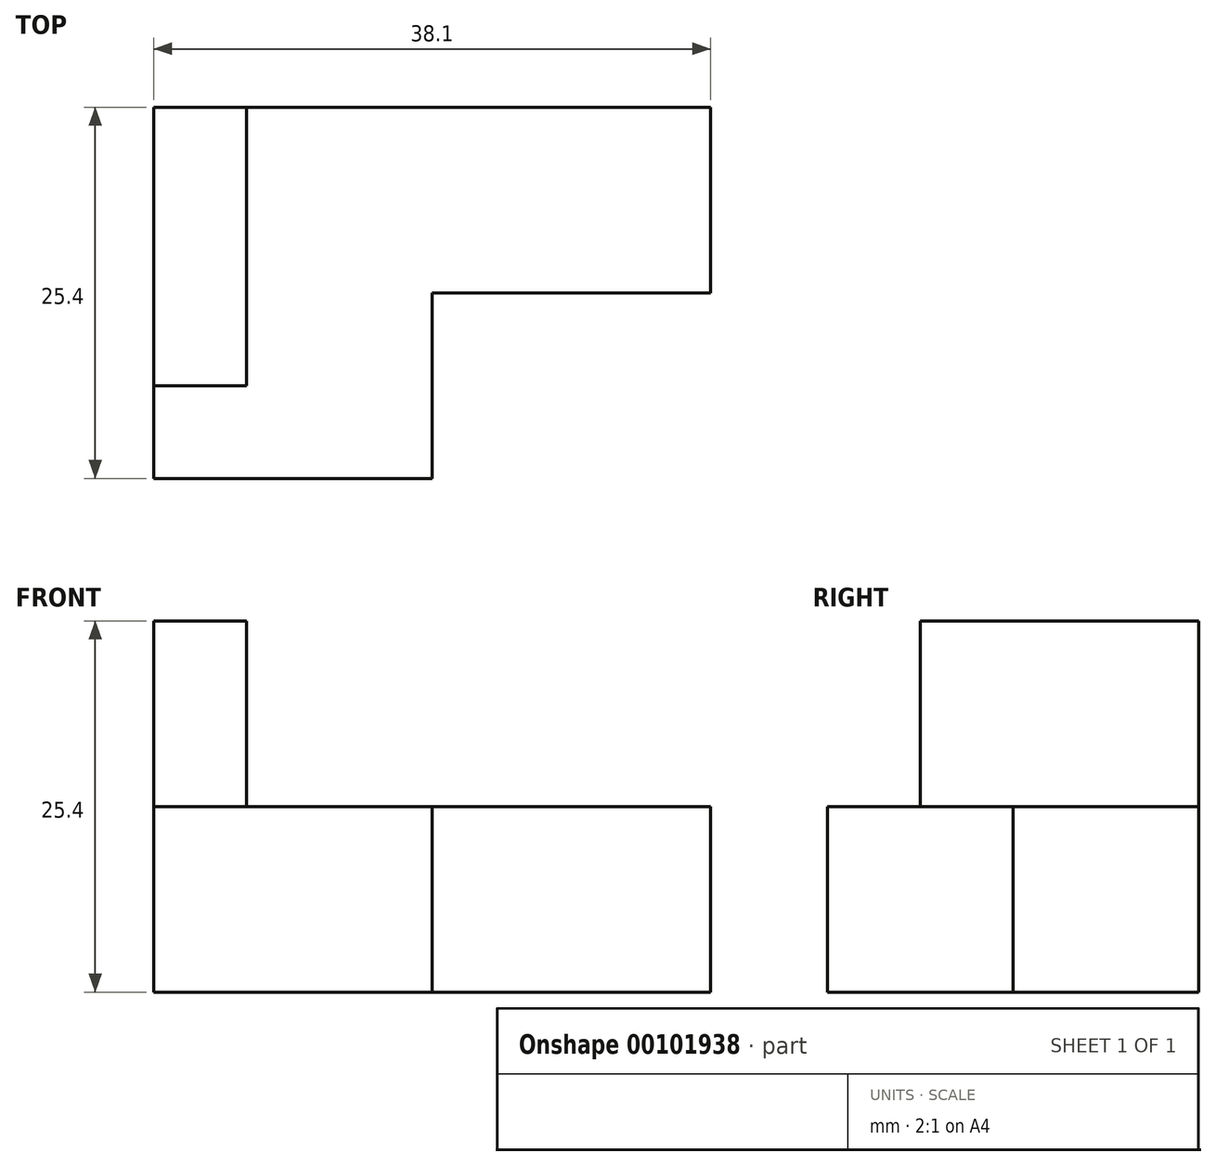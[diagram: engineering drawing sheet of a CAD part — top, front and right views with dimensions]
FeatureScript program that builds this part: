
annotation { "Feature Type Name" : "Feature", "Feature Type Description" : "" }
export const myFeature = defineFeature(function(context is Context, id is Id, definition is map)
    precondition{}
    {
        {
            var Q0;
            Q0=qCreatedBy(makeId("Front.planeOp"),FACE);
            var sketch = newSketch(context, id + "F0", { "sketchPlane" : qUnion([Q0])});
            skLineSegment(sketch, "E0", {"start": v(0, 0) * mm, "end": v(38.1, 0) * mm});
            skLineSegment(sketch, "E1", {"start": v(38.1, 0) * mm, "end": v(38.1, 12.7) * mm});
            skLineSegment(sketch, "E2", {"start": v(38.1, 12.7) * mm, "end": v(6.35, 12.7) * mm});
            skLineSegment(sketch, "E3", {"start": v(6.35, 12.7) * mm, "end": v(6.35, 25.4) * mm});
            skLineSegment(sketch, "E4", {"start": v(6.35, 25.4) * mm, "end": v(0, 25.4) * mm});
            skLineSegment(sketch, "E5", {"start": v(0, 25.4) * mm, "end": v(0, 0) * mm});
            skSolve(sketch);
        }
        {
            var Q0;
            Q0 = qSketchRegion(id + "F0", true);
            extrude(context, id + "F1", {"entities" : qUnion([Q0]), "endBound" : BoundingType.SYMMETRIC, "depth" : 25.4 * mm});
        }
        {
            var Q0;
            Q0=makeQuery(id+"F1.opExtrude","SWEPT_FACE",FACE,{"disambiguationData":[OSD([sQuery(id+"F0.wireOp",EDGE,"E2")])]});
            var sketch = newSketch(context, id + "F2", { "sketchPlane" : qUnion([Q0])});
            skLineSegment(sketch, "E6.bottom", {"start": v(38.1, -12.7) * mm, "end": v(19.05, -12.7) * mm});
            skLineSegment(sketch, "E6.top", {"start": v(38.1, 0) * mm, "end": v(19.05, 0) * mm});
            skLineSegment(sketch, "E6.left", {"start": v(38.1, -12.7) * mm, "end": v(38.1, 0) * mm});
            skLineSegment(sketch, "E6.right", {"start": v(19.05, -12.7) * mm, "end": v(19.05, 0) * mm});
            skSolve(sketch);
        }
        {
            var Q0;
            Q0=makeQuery(id+"F2.imprint","IMPRINT",FACE,{"disambiguationData":[TD([[makeQuery(id+"F2.imprint","IMPRINT",EDGE,{"derivedFrom":sQuery(id+"F2.wireOp",EDGE,"E6.bottom")}),-1.0]])]});
            extrude(context, id + "F3", {"entities" : qUnion([Q0]), "operationType" : NewBodyOperationType.REMOVE, "endBound" : BoundingType.THROUGH_ALL, "oppositeDirection" : true, "depth" : 25.4 * mm});
        }
        {
            var Q0;
            Q0=makeQuery(id+"F1.opExtrude","SWEPT_FACE",FACE,{"disambiguationData":[OSD([sQuery(id+"F0.wireOp",EDGE,"E3")])]});
            var sketch = newSketch(context, id + "F4", { "sketchPlane" : qUnion([Q0])});
            skLineSegment(sketch, "E7.bottom", {"start": v(-12.7, 25.4) * mm, "end": v(-6.35, 25.4) * mm});
            skLineSegment(sketch, "E7.top", {"start": v(-12.7, 12.7) * mm, "end": v(-6.35, 12.7) * mm});
            skLineSegment(sketch, "E7.left", {"start": v(-12.7, 25.4) * mm, "end": v(-12.7, 12.7) * mm});
            skLineSegment(sketch, "E7.right", {"start": v(-6.35, 25.4) * mm, "end": v(-6.35, 12.7) * mm});
            skSolve(sketch);
        }
        {
            var Q0;
            Q0 = qSketchRegion(id + "F4", true);
            extrude(context, id + "F5", {"entities" : qUnion([Q0]), "operationType" : NewBodyOperationType.REMOVE, "endBound" : BoundingType.THROUGH_ALL, "oppositeDirection" : true, "depth" : 25.4 * mm});
        }
    });
